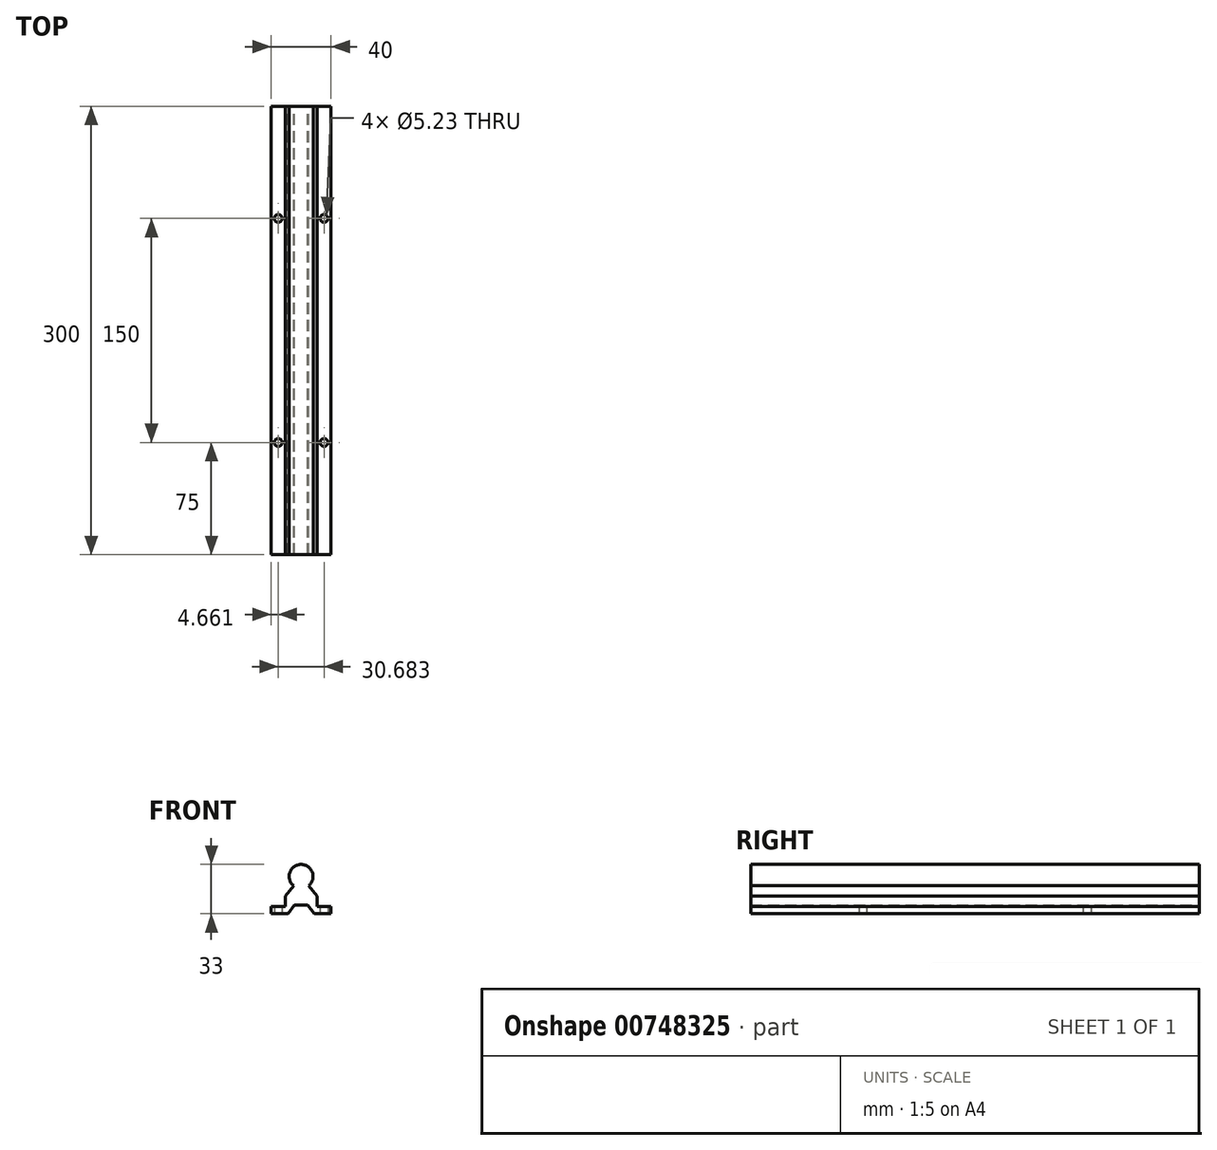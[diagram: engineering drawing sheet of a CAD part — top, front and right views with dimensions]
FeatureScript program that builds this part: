
annotation { "Feature Type Name" : "Feature", "Feature Type Description" : "" }
export const myFeature = defineFeature(function(context is Context, id is Id, definition is map)
    precondition{}
    {
        {
            var Q0;
            Q0=qCreatedBy(makeId("Front.planeOp"),FACE);
            var sketch = newSketch(context, id + "F0", { "sketchPlane" : qUnion([Q0])});
            skCircle(sketch, "E0", {"center": v(0, 0) * mm, "radius": 8 * mm});
            skLineSegment(sketch, "E1", {"start": v(0, 10.3) * mm, "end": v(0, -10.85) * mm, "construction": true});
            skLineSegment(sketch, "E2", {"start": v(12.1, 0) * mm, "end": v(-10.9, 0) * mm, "construction": true});
            skLineSegment(sketch, "E3", {"start": v(-5, -6.24) * mm, "end": v(-10.67, -13) * mm});
            skLineSegment(sketch, "E4", {"start": v(-10.67, -13) * mm, "end": v(-10.67, -20) * mm});
            skLineSegment(sketch, "E5", {"start": v(-10.67, -20) * mm, "end": v(-20, -20) * mm});
            skLineSegment(sketch, "E6", {"start": v(-20, -20) * mm, "end": v(-20, -25) * mm});
            skLineSegment(sketch, "E7", {"start": v(-20, -25) * mm, "end": v(-8.73, -25) * mm});
            skLineSegment(sketch, "E8", {"start": v(20, -25) * mm, "end": v(20, -20) * mm});
            skLineSegment(sketch, "E9", {"start": v(20, -20) * mm, "end": v(16.54, -20) * mm});
            skLineSegment(sketch, "E10", {"start": v(10.67, -13) * mm, "end": v(5, -6.24) * mm});
            skLineSegment(sketch, "E11", {"start": v(10.67, -13) * mm, "end": v(10.67, -20) * mm});
            skLineSegment(sketch, "E12", {"start": v(10.67, -20) * mm, "end": v(16.54, -20) * mm});
            skLineSegment(sketch, "E13", {"start": v(0, -10.85) * mm, "end": v(0, -25) * mm, "construction": true});
            skLineSegment(sketch, "E14.0", {"start": v(-4.44, -10.85) * mm, "end": v(-4.44, -25) * mm, "construction": true});
            skLineSegment(sketch, "E15.0", {"start": v(4.45, -10.85) * mm, "end": v(4.45, -25) * mm, "construction": true});
            skLineSegment(sketch, "E16.bottom", {"start": v(8.73, -30.73) * mm, "end": v(-8.73, -30.73) * mm, "construction": true});
            skLineSegment(sketch, "E16.top", {"start": v(8.73, -19.27) * mm, "end": v(-8.73, -19.27) * mm, "construction": true});
            skLineSegment(sketch, "E16.left", {"start": v(8.73, -30.73) * mm, "end": v(8.73, -19.27) * mm, "construction": true});
            skLineSegment(sketch, "E16.right", {"start": v(-8.73, -30.73) * mm, "end": v(-8.73, -19.27) * mm, "construction": true});
            skPoint(sketch, "E16.middle", {"position": v(0, -25) * mm});
            skLineSegment(sketch, "E17", {"start": v(-8.73, -25) * mm, "end": v(-4.44, -19.27) * mm});
            skLineSegment(sketch, "E18", {"start": v(-4.44, -19.27) * mm, "end": v(4.45, -19.27) * mm});
            skLineSegment(sketch, "E19", {"start": v(4.45, -19.27) * mm, "end": v(8.73, -25) * mm});
            skLineSegment(sketch, "E20.trimOffspring", {"start": v(8.73, -25) * mm, "end": v(20, -25) * mm});
            skSolve(sketch);
        }
        {
            var Q0;
            Q0=qSketchRegion(id+"F0",true);
            extrude(context, id + "F1", {"entities" : qUnion([Q0]), "depth" : 300 * mm, "offsetDistance" : 25.4 * mm});
        }
        {
            var Q0;
            {var subQ5=sQuery(id+"F0.wireOp",EDGE,"E7");var subQ6=sQuery(id+"F0.wireOp",EDGE,"E6");Q0=makeQuery(id+"FOCyhoGR0N8pPDN_1.boolean.opBoolean","SPLIT",FACE,{"disambiguationData":[TD([makeQuery(id+"F1.opExtrude","SWEPT_FACE",FACE,{"disambiguationData":[OSD([subQ6])]})])],"derivedFrom":makeQuery(id+"F1.opExtrude","SWEPT_FACE",FACE,{"disambiguationData":[OSD([subQ5])]})});}
            var sketch = newSketch(context, id + "F2", { "sketchPlane" : qUnion([Q0])});
            skLineSegment(sketch, "E21", {"start": v(-20, 150) * mm, "end": v(-15.34, 150) * mm, "construction": true});
            skLineSegment(sketch, "E22", {"start": v(-15.34, 150) * mm, "end": v(15.34, 150) * mm, "construction": true});
            skLineSegment(sketch, "E23.0", {"start": v(-15.34, 75) * mm, "end": v(15.34, 75) * mm, "construction": true});
            skLineSegment(sketch, "E24.0", {"start": v(-15.34, 225) * mm, "end": v(15.34, 225) * mm, "construction": true});
            skCircle(sketch, "E25", {"center": v(15.34, 225) * mm, "radius": 2.62 * mm});
            skCircle(sketch, "E26", {"center": v(-15.34, 225) * mm, "radius": 2.62 * mm});
            skCircle(sketch, "E27", {"center": v(15.34, 75) * mm, "radius": 2.62 * mm});
            skCircle(sketch, "E28", {"center": v(-15.34, 75) * mm, "radius": 2.62 * mm});
            skSolve(sketch);
        }
        {
            var Q0;
            Q0 = qSketchRegion(id + "F2", true);
            extrude(context, id + "F3", {"entities" : qUnion([Q0]), "operationType" : NewBodyOperationType.REMOVE, "endBound" : BoundingType.THROUGH_ALL, "oppositeDirection" : true, "depth" : 25.4 * mm, "offsetDistance" : 25.4 * mm});
        }
    });
